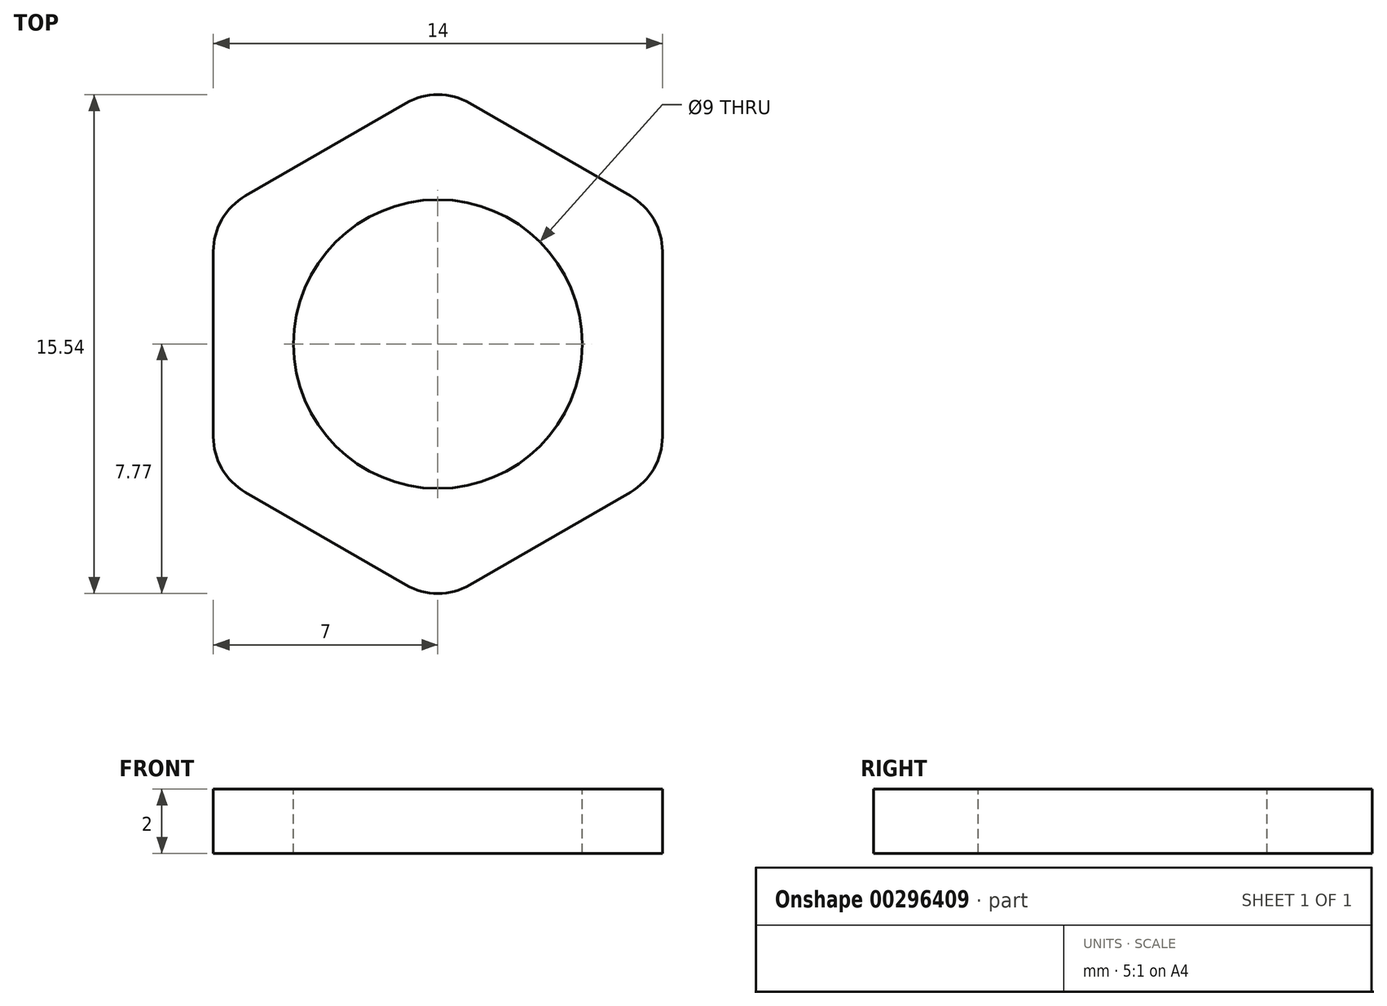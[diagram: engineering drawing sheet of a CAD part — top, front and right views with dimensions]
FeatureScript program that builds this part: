
annotation { "Feature Type Name" : "Feature", "Feature Type Description" : "" }
export const myFeature = defineFeature(function(context is Context, id is Id, definition is map)
    precondition{}
    {
        {
            var Q0;
            Q0=qCreatedBy(makeId("Top.planeOp"),FACE);
            var sketch = newSketch(context, id + "F0", { "sketchPlane" : qUnion([Q0])});
            skCircle(sketch, "E0.cCircle", {"center": v(0, 0) * mm, "radius": 7 * mm, "construction": true});
            skLineSegment(sketch, "E0.0", {"start": v(7, -4.04) * mm, "end": v(0, -8.08) * mm});
            skLineSegment(sketch, "E0.1", {"start": v(0, -8.08) * mm, "end": v(-7, -4.04) * mm});
            skLineSegment(sketch, "E0.2", {"start": v(-7, -4.04) * mm, "end": v(-7, 4.04) * mm});
            skLineSegment(sketch, "E0.3", {"start": v(-7, 4.04) * mm, "end": v(0, 8.08) * mm});
            skLineSegment(sketch, "E0.4", {"start": v(0, 8.08) * mm, "end": v(7, 4.04) * mm});
            skLineSegment(sketch, "E0.5", {"start": v(7, 4.04) * mm, "end": v(7, -4.04) * mm});
            skPoint(sketch, "E0.0.midPoint", {"position": v(3.5, -6.06) * mm});
            skCircle(sketch, "E1", {"center": v(0, 0) * mm, "radius": 5 * mm});
            skSolve(sketch);
        }
        {
            var Q0;
            Q0 = qSketchRegion(id + "F0", true);
            var Q1;
            Q1=makeQuery(id+"F0.imprint","IMPRINT",FACE,{"disambiguationData":[TD([[makeQuery(id+"F0.imprint","IMPRINT",EDGE,{"derivedFrom":sQuery(id+"F0.wireOp",EDGE,"E1")}),1.0]])]});
            extrude(context, id + "F1", {"entities" : qUnion([Q0, Q1]), "depth" : 2 * mm, "offsetDistance" : 25 * mm});
        }
        {
            var Q0;
            Q0=sQuery(id+"F0.wireOp",VERTEX,"E0.cCircle.center");
            var Q1;
            Q1=makeQuery(id+"F1.opExtrude","SWEPT_BODY",BODY,{"disambiguationData":[OSD([sQuery(id+"F0.wireOp",EDGE,"E0.0"),sQuery(id+"F0.wireOp",EDGE,"E0.1"),sQuery(id+"F0.wireOp",EDGE,"E0.2"),sQuery(id+"F0.wireOp",EDGE,"E0.3"),sQuery(id+"F0.wireOp",EDGE,"E0.4"),sQuery(id+"F0.wireOp",EDGE,"E0.5")])]});
            hole(context, id + "F2", {"style" : HoleStyle.SIMPLE, "endStyle" : HoleEndStyle.THROUGH, "oppositeDirection" : true, "standardTappedOrClearance" : lookupTablePath({ "standard" : "ISO", "engagement" : "75%", "pitch" : "1 mm", "size" : "M10", "type" : "Tapped" }), "standardBlindInLast" : lookupTablePath({ "standard" : "ISO", "engagement" : "75%", "pitch" : "1 mm", "size" : "M10", "type" : "Tapped" }), "holeDiameter" : 9 * mm, "majorDiameter" : 10 * mm, "showTappedDepth" : true, "isTappedThrough" : true, "tappedDepth" : 12 * mm, "tapClearance" : 3, "locations" : qUnion([Q0]), "scope" : qUnion([Q1])});
        }
        {
            var Q0;
            Q0=makeQuery(id+"F1.opExtrude","SWEPT_EDGE",EDGE,{"disambiguationData":[OSD([sQuery(id+"F0.wireOp",EDGE,"E0.0"),sQuery(id+"F0.wireOp",EDGE,"E0.1")])]});
            var Q1;
            Q1=makeQuery(id+"F1.opExtrude","SWEPT_EDGE",EDGE,{"disambiguationData":[OSD([sQuery(id+"F0.wireOp",EDGE,"E0.0"),sQuery(id+"F0.wireOp",EDGE,"E0.5")])]});
            var Q2;
            Q2=makeQuery(id+"F1.opExtrude","SWEPT_EDGE",EDGE,{"disambiguationData":[OSD([sQuery(id+"F0.wireOp",EDGE,"E0.4"),sQuery(id+"F0.wireOp",EDGE,"E0.5")])]});
            var Q3;
            Q3=makeQuery(id+"F1.opExtrude","SWEPT_EDGE",EDGE,{"disambiguationData":[OSD([sQuery(id+"F0.wireOp",EDGE,"E0.3"),sQuery(id+"F0.wireOp",EDGE,"E0.4")])]});
            var Q4;
            Q4=makeQuery(id+"F1.opExtrude","SWEPT_EDGE",EDGE,{"disambiguationData":[OSD([sQuery(id+"F0.wireOp",EDGE,"E0.2"),sQuery(id+"F0.wireOp",EDGE,"E0.3")])]});
            var Q5;
            Q5=makeQuery(id+"F1.opExtrude","SWEPT_EDGE",EDGE,{"disambiguationData":[OSD([sQuery(id+"F0.wireOp",EDGE,"E0.1"),sQuery(id+"F0.wireOp",EDGE,"E0.2")])]});
            fillet(context, id + "F3", {"entities" : qUnion([Q0, Q1, Q2, Q3, Q4, Q5]), "radius" : 2 * mm, "tangentPropagation" : true, "allowEdgeOverflow" : false});
        }
    });
